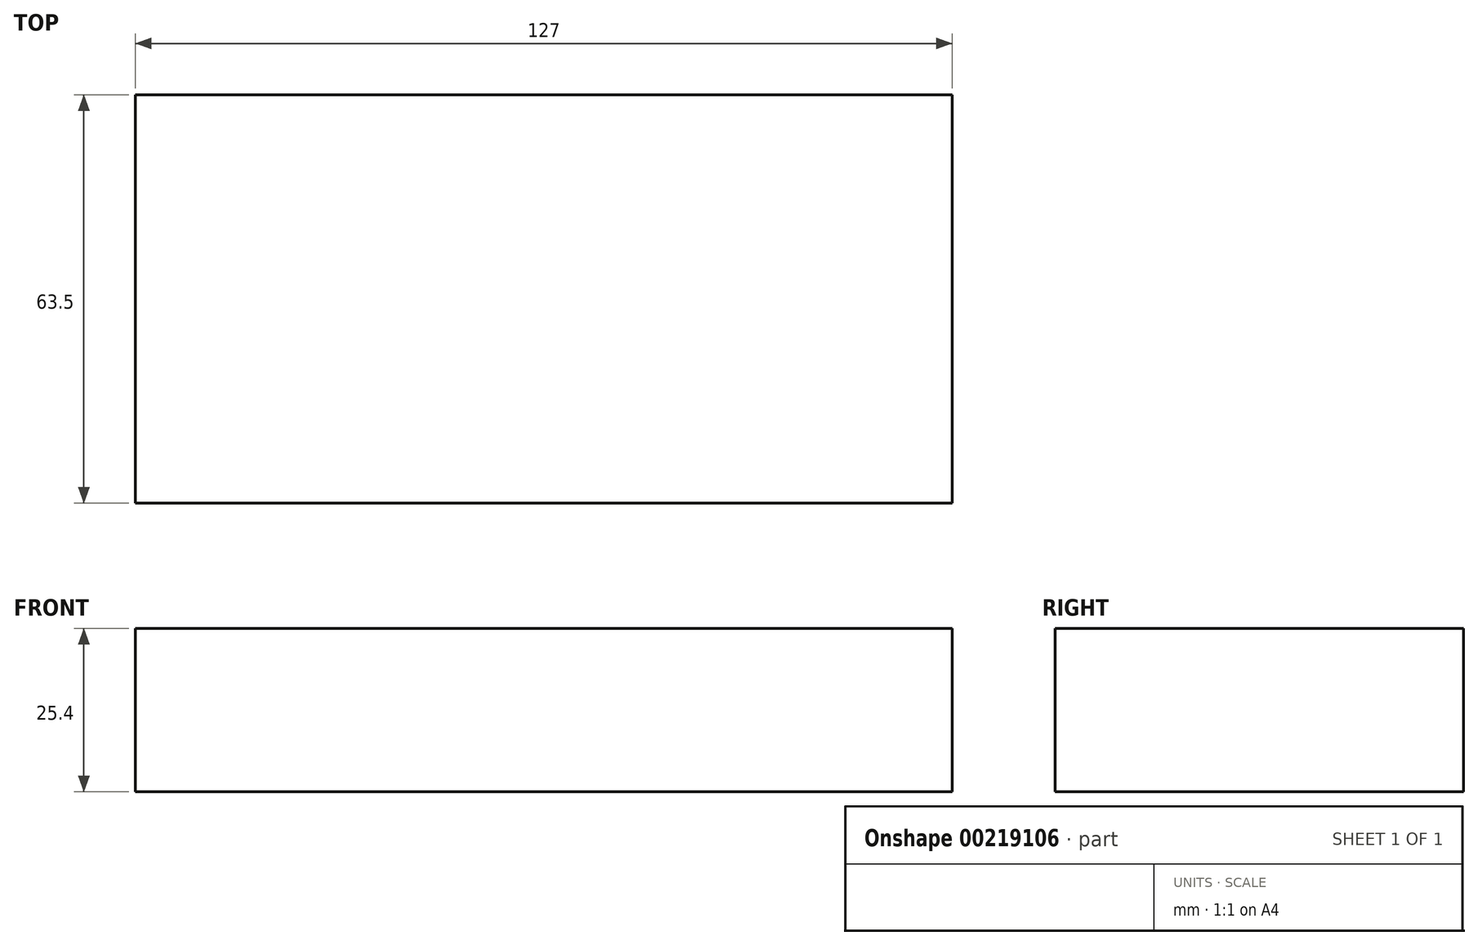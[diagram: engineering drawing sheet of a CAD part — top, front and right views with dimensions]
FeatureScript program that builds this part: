
annotation { "Feature Type Name" : "Feature", "Feature Type Description" : "" }
export const myFeature = defineFeature(function(context is Context, id is Id, definition is map)
    precondition{}
    {
        {
            var Q0;
            Q0=qCreatedBy(makeId("Top.planeOp"),FACE);
            var sketch = newSketch(context, id + "F0", { "sketchPlane" : qUnion([Q0])});
            skLineSegment(sketch, "E0.bottom", {"start": v(-58.16, 31.75) * mm, "end": v(68.84, 31.75) * mm});
            skLineSegment(sketch, "E0.top", {"start": v(-58.16, -31.75) * mm, "end": v(68.84, -31.75) * mm});
            skLineSegment(sketch, "E0.left", {"start": v(-58.16, 31.75) * mm, "end": v(-58.16, -31.75) * mm});
            skLineSegment(sketch, "E0.right", {"start": v(68.84, 31.75) * mm, "end": v(68.84, -31.75) * mm});
            skLineSegment(sketch, "E1", {"start": v(-58.16, 0) * mm, "end": v(-123.12, 0) * mm, "construction": true});
            skSolve(sketch);
        }
        {
            var Q0;
            Q0=makeQuery(id+"F0.imprint","IMPRINT",FACE,{"disambiguationData":[TD([[makeQuery(id+"F0.imprint","IMPRINT",EDGE,{"derivedFrom":sQuery(id+"F0.wireOp",EDGE,"E0.bottom")}),-1.0]])]});
            extrude(context, id + "F1", {"entities" : qUnion([Q0]), "endBound" : BoundingType.SYMMETRIC, "depth" : 25.4 * mm});
        }
    });
